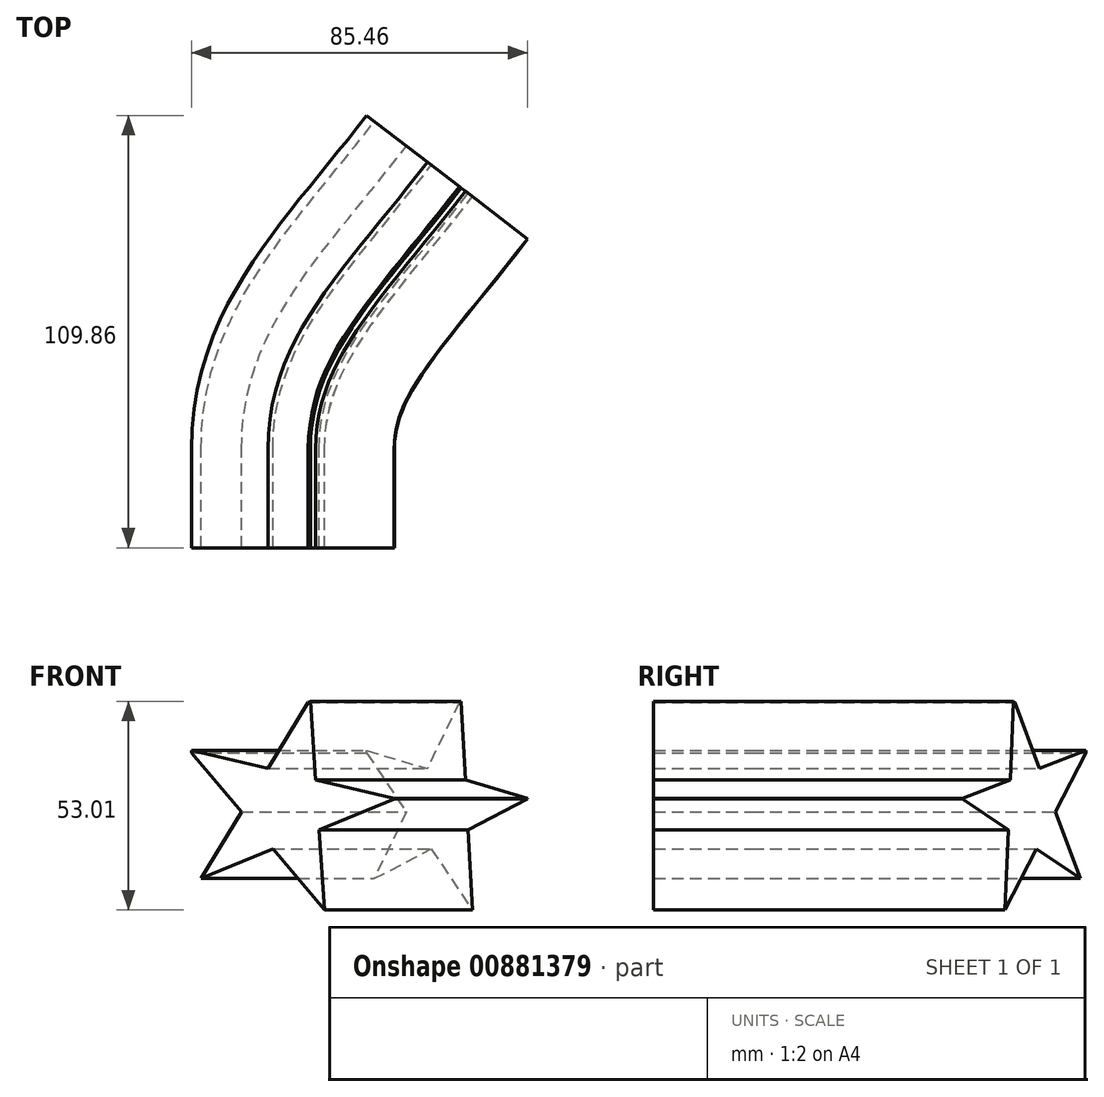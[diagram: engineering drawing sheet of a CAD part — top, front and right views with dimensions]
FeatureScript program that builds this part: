
annotation { "Feature Type Name" : "Feature", "Feature Type Description" : "" }
export const myFeature = defineFeature(function(context is Context, id is Id, definition is map)
    precondition{}
    {
        {
            var Q0;
            Q0=qCreatedBy(makeId("Front.planeOp"),FACE);
            var sketch = newSketch(context, id + "F0", { "sketchPlane" : qUnion([Q0])});
            skCircle(sketch, "E0.cCircle", {"center": v(0, 0) * mm, "radius": 28.1 * mm, "construction": true});
            skLineSegment(sketch, "E0.0", {"start": v(-23.89, 14.8) * mm, "end": v(6.69, 27.29) * mm});
            skLineSegment(sketch, "E0.1", {"start": v(6.69, 27.29) * mm, "end": v(28.02, 2.07) * mm});
            skLineSegment(sketch, "E0.2", {"start": v(28.02, 2.07) * mm, "end": v(10.63, -26) * mm});
            skLineSegment(sketch, "E0.3", {"start": v(10.63, -26) * mm, "end": v(-21.45, -18.15) * mm});
            skLineSegment(sketch, "E0.4", {"start": v(-21.45, -18.15) * mm, "end": v(-23.89, 14.8) * mm});
            skSolve(sketch);
        }
        {
            var Q0;
            Q0=makeQuery(id+"F0.imprint","IMPRINT",FACE,{"disambiguationData":[TD([[makeQuery(id+"F0.imprint","IMPRINT",EDGE,{"derivedFrom":sQuery(id+"F0.wireOp",EDGE,"E0.0")}),-1.0]])]});
            var sketch = newSketch(context, id + "F1", { "sketchPlane" : qUnion([Q0])});
            skLineSegment(sketch, "E1", {"start": v(-24.5, 14.8) * mm, "end": v(27.9, 2.47) * mm});
            skLineSegment(sketch, "E2", {"start": v(6.32, 27.74) * mm, "end": v(-21.42, -17.88) * mm});
            skLineSegment(sketch, "E3", {"start": v(-24.5, 14.8) * mm, "end": v(10.02, -25.9) * mm});
            skLineSegment(sketch, "E4", {"start": v(6.32, 27.74) * mm, "end": v(10.02, -25.9) * mm});
            skLineSegment(sketch, "E5", {"start": v(-21.42, -17.88) * mm, "end": v(27.9, 2.47) * mm});
            skSolve(sketch);
        }
        {
            var Q0;
            {var subQ0=sQuery(id+"F1.wireOp",EDGE,"E2");var subQ1=sQuery(id+"F1.wireOp",EDGE,"E1");var subQ2=makeQuery(id+"F1.imprint","INTERSECT",VERTEX,{"derivedFrom":[subQ1,subQ0]});Q0=makeQuery(id+"F1.imprint","IMPRINT",FACE,{"disambiguationData":[TD([[makeQuery(id+"F1.imprint","IMPRINT",EDGE,{"disambiguationData":[TD([[subQ2,-1.0]])],"derivedFrom":subQ1}),1.0]])]});}
            var Q1;
            {var subQ0=sQuery(id+"F1.wireOp",EDGE,"E2");var subQ1=sQuery(id+"F1.wireOp",EDGE,"E1");var subQ2=makeQuery(id+"F1.imprint","INTERSECT",VERTEX,{"derivedFrom":[subQ1,subQ0]});Q1=makeQuery(id+"F1.imprint","IMPRINT",FACE,{"disambiguationData":[TD([[makeQuery(id+"F1.imprint","IMPRINT",EDGE,{"disambiguationData":[TD([[subQ2,1.0]])],"derivedFrom":subQ1}),-1.0]])]});}
            var Q2;
            {var subQ0=sQuery(id+"F1.wireOp",EDGE,"E4");var subQ1=sQuery(id+"F1.wireOp",EDGE,"E1");var subQ2=makeQuery(id+"F1.imprint","INTERSECT",VERTEX,{"derivedFrom":[subQ1,subQ0]});Q2=makeQuery(id+"F1.imprint","IMPRINT",FACE,{"disambiguationData":[TD([[makeQuery(id+"F1.imprint","IMPRINT",EDGE,{"disambiguationData":[TD([[subQ2,-1.0]])],"derivedFrom":subQ1}),-1.0]])]});}
            var Q3;
            {var subQ1=sQuery(id+"F1.wireOp",EDGE,"E1");var subQ6=sQuery(id+"F1.wireOp",EDGE,"E2");var subQ9=makeQuery(id+"F1.imprint","INTERSECT",VERTEX,{"derivedFrom":[subQ1,subQ6]});Q3=makeQuery(id+"F1.imprint","IMPRINT",FACE,{"disambiguationData":[TD([[makeQuery(id+"F1.imprint","IMPRINT",EDGE,{"disambiguationData":[TD([[subQ9,-1.0]])],"derivedFrom":subQ1}),-1.0]])]});}
            var Q4;
            {var subQ0=sQuery(id+"F1.wireOp",EDGE,"E5");var subQ1=sQuery(id+"F1.wireOp",EDGE,"E3");var subQ2=makeQuery(id+"F1.imprint","INTERSECT",VERTEX,{"derivedFrom":[subQ1,subQ0]});Q4=makeQuery(id+"F1.imprint","IMPRINT",FACE,{"disambiguationData":[TD([[makeQuery(id+"F1.imprint","IMPRINT",EDGE,{"disambiguationData":[TD([[subQ2,-1.0]])],"derivedFrom":subQ1}),1.0]])]});}
            var Q5;
            {var subQ0=sQuery(id+"F1.wireOp",EDGE,"E5");var subQ1=sQuery(id+"F1.wireOp",EDGE,"E2");var subQ2=makeQuery(id+"F1.imprint","INTERSECT",VERTEX,{"derivedFrom":[subQ1,subQ0]});Q5=makeQuery(id+"F1.imprint","IMPRINT",FACE,{"disambiguationData":[TD([[makeQuery(id+"F1.imprint","IMPRINT",EDGE,{"disambiguationData":[TD([[subQ2,1.0]])],"derivedFrom":subQ1}),1.0]])]});}
            extrude(context, id + "F2", {"entities" : qUnion([Q0, Q1, Q2, Q3, Q4, Q5]), "depth" : 25 * mm, "offsetDistance" : 25 * mm});
        }
        {
            var Q0;
            Q0=qCreatedBy(makeId("Top.planeOp"),FACE);
            var sketch = newSketch(context, id + "F3", { "sketchPlane" : qUnion([Q0])});
            skFitSpline(sketch, "E6", {"points": [v(0, 0) * mm, v(11.22, 33.76) * mm, v(39.58, 70.31) * mm], "startDerivative": vector(0, 85.32) * mm, "endDerivative": vector(58.18, 75.72) * mm});
            skSolve(sketch);
        }
        {
            var Q0;
            Q0=makeQuery(id+"F2.opExtrude","CAP_FACE",FACE,{"disambiguationData":[OSD([sQuery(id+"F0.wireOp",EDGE,"E0.0"),sQuery(id+"F0.wireOp",EDGE,"E0.1"),sQuery(id+"F0.wireOp",EDGE,"E0.3"),sQuery(id+"F0.wireOp",EDGE,"E0.4"),sQuery(id+"F1.wireOp",EDGE,"E1"),sQuery(id+"F1.wireOp",EDGE,"E2"),sQuery(id+"F1.wireOp",EDGE,"E3"),sQuery(id+"F1.wireOp",EDGE,"E4"),sQuery(id+"F1.wireOp",EDGE,"E5")])],"isStart":true});
            var Q1;
            Q1=sQuery(id+"F3.wireOp",EDGE,"E6");
            sweep(context, id + "F4", {"operationType" : NewBodyOperationType.ADD, "profiles" : qUnion([Q0]), "path" : qUnion([Q1])});
        }
    });
